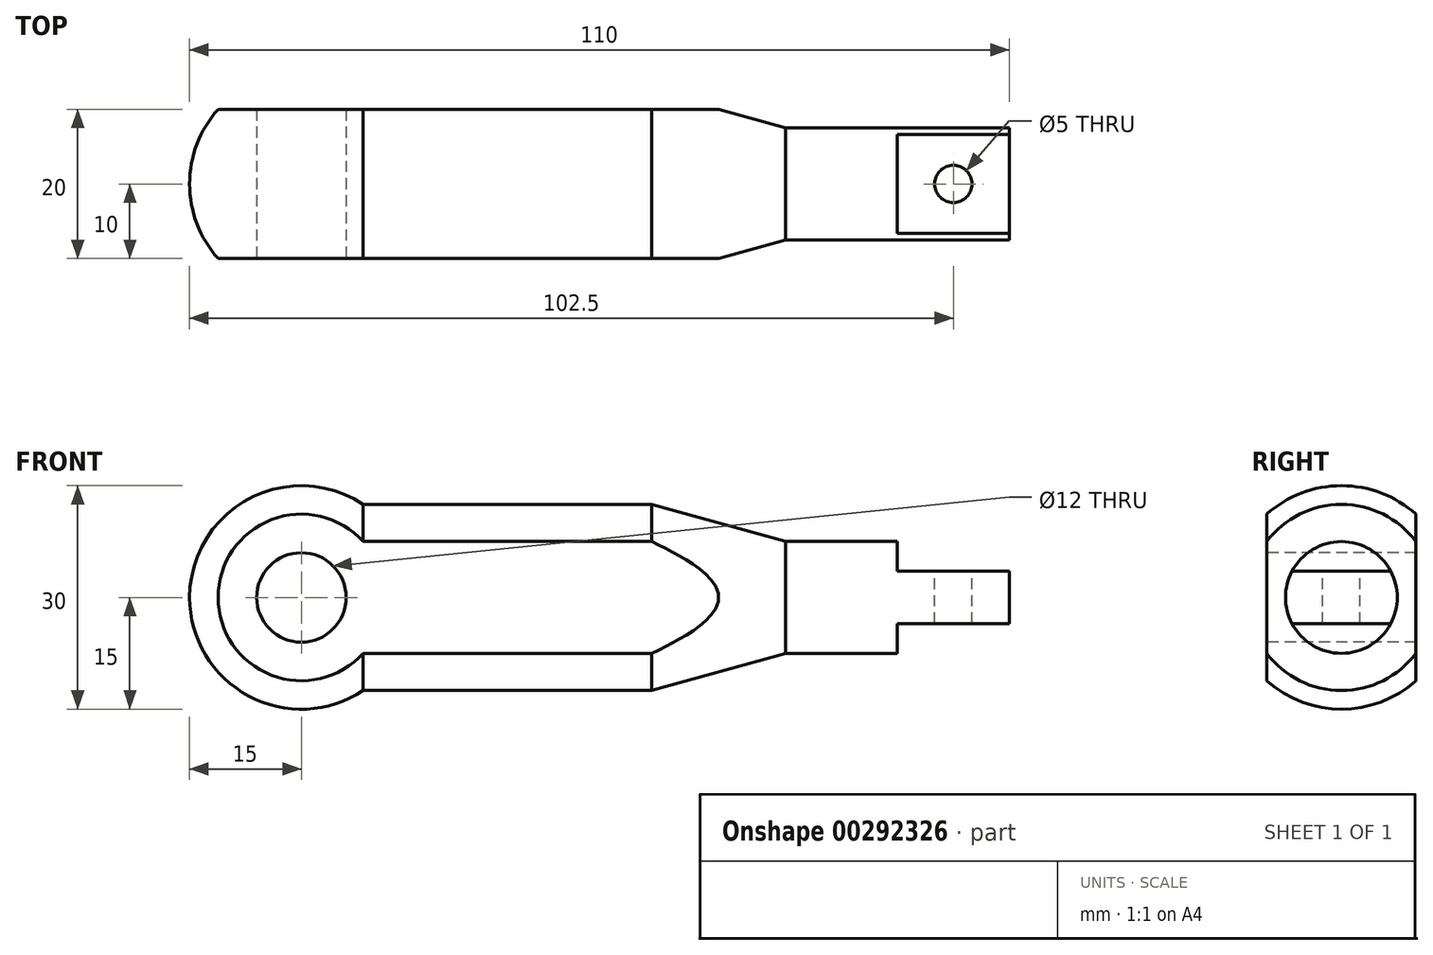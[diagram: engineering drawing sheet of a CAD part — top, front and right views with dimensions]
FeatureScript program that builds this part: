
annotation { "Feature Type Name" : "Feature", "Feature Type Description" : "" }
export const myFeature = defineFeature(function(context is Context, id is Id, definition is map)
    precondition{}
    {
        {
            var Q0;
            Q0=qCreatedBy(makeId("Front.planeOp"),FACE);
            var sketch = newSketch(context, id + "F0", { "sketchPlane" : qUnion([Q0])});
            skLineSegment(sketch, "E0", {"start": v(0, 0) * mm, "end": v(73.31, 0) * mm, "construction": true});
            skArc(sketch, "E1", {"start": v(-15, 0) * mm, "mid": v(-7.1, 13.22) * mm, "end": v(8.3, 12.5) * mm});
            skLineSegment(sketch, "E2", {"start": v(95, 7.5) * mm, "end": v(95, 0) * mm});
            skLineSegment(sketch, "E3", {"start": v(95, 0) * mm, "end": v(-15, 0) * mm});
            skLineSegment(sketch, "E4", {"start": v(8.3, 12.5) * mm, "end": v(47, 12.5) * mm});
            skLineSegment(sketch, "E5", {"start": v(47, 12.5) * mm, "end": v(65, 7.5) * mm});
            skLineSegment(sketch, "E6", {"start": v(65, 7.5) * mm, "end": v(95, 7.5) * mm});
            skSolve(sketch);
        }
        {
            var Q0;
            Q0 = qSketchRegion(id + "F0", true);
            var Q1;
            Q1=sQuery(id+"F0.wireOp",EDGE,"E3");
            revolve(context, id + "F1", {"entities" : qUnion([Q0]), "axis" : qUnion([Q1]), "revolveType" : RevolveType.FULL});
        }
        {
            var Q0;
            Q0=qCreatedBy(makeId("Front.planeOp"),FACE);
            var sketch = newSketch(context, id + "F2", { "sketchPlane" : qUnion([Q0])});
            skLineSegment(sketch, "E7.top", {"start": v(95, 3.5) * mm, "end": v(80, 3.5) * mm});
            skLineSegment(sketch, "E7.left", {"start": v(95, 7.5) * mm, "end": v(95, 3.5) * mm});
            skLineSegment(sketch, "E7.right", {"start": v(80, 7.5) * mm, "end": v(80, 3.5) * mm});
            skLineSegment(sketch, "E8", {"start": v(95, -7.5) * mm, "end": v(65, -7.5) * mm});
            skLineSegment(sketch, "E9", {"start": v(65, 7.5) * mm, "end": v(95, 7.5) * mm});
            skLineSegment(sketch, "E10", {"start": v(80, 7.5) * mm, "end": v(95, 7.5) * mm});
            skLineSegment(sketch, "E11", {"start": v(74.8, 0) * mm, "end": v(95.87, 0) * mm});
            skLineSegment(sketch, "E12.MirrorCS", {"start": v(95, -3.5) * mm, "end": v(80, -3.5) * mm});
            skLineSegment(sketch, "E13.MirrorCS", {"start": v(80, -7.5) * mm, "end": v(80, -3.5) * mm});
            skLineSegment(sketch, "E14.MirrorCS", {"start": v(95, -7.5) * mm, "end": v(95, -3.5) * mm});
            skLineSegment(sketch, "E15.MirrorCS", {"start": v(80, -7.5) * mm, "end": v(95, -7.5) * mm});
            skSolve(sketch);
        }
        {
            var Q0;
            Q0 = qSketchRegion(id + "F2", true);
            extrude(context, id + "F3", {"entities" : qUnion([Q0]), "operationType" : NewBodyOperationType.REMOVE, "endBound" : BoundingType.THROUGH_ALL, "oppositeDirection" : true, "depth" : 25 * mm, "hasSecondDirection" : true, "secondDirectionBound" : SecondDirectionBoundingType.THROUGH_ALL, "secondDirectionOppositeDirection" : false, "secondDirectionDepth" : 25 * mm});
        }
        {
            var Q0;
            Q0=makeQuery(id+"F1.opRevolve","SWEPT_FACE",FACE,{"disambiguationData":[OSD([sQuery(id+"F0.wireOp",EDGE,"E2")])]});
            var sketch = newSketch(context, id + "F4", { "sketchPlane" : qUnion([Q0])});
            skLineSegment(sketch, "E16", {"start": v(-10, 11.18) * mm, "end": v(-10, -11.18) * mm});
            skCircle(sketch, "E17", {"center": v(0, 0) * mm, "radius": 15 * mm});
            skLineSegment(sketch, "E18", {"start": v(10, 11.18) * mm, "end": v(10, -11.18) * mm});
            skLineSegment(sketch, "E19", {"start": v(0, 19.8) * mm, "end": v(0, -19.84) * mm, "construction": true});
            skArc(sketch, "E20", {"start": v(-10, 11.18) * mm, "mid": v(-15, 0) * mm, "end": v(-10, -11.18) * mm});
            skArc(sketch, "E21", {"start": v(10, -11.18) * mm, "mid": v(15, 0) * mm, "end": v(10, 11.18) * mm});
            skSolve(sketch);
        }
        {
            var Q0;
            {var subQ0=sQuery(id+"F4.wireOp",EDGE,"E16");Q0=makeQuery(id+"F4.imprint","IMPRINT",FACE,{"disambiguationData":[TD([[makeQuery(id+"F4.imprint","IMPRINT",EDGE,{"derivedFrom":subQ0}),-1.0]])]});}
            var Q1;
            {var subQ0=sQuery(id+"F4.wireOp",EDGE,"E18");Q1=makeQuery(id+"F4.imprint","IMPRINT",FACE,{"disambiguationData":[TD([[makeQuery(id+"F4.imprint","IMPRINT",EDGE,{"derivedFrom":subQ0}),1.0]])]});}
            var Q2;
            Q2=sQuery(id+"F4.wireOp",EDGE,"E21");
            var Q3;
            Q3=sQuery(id+"F4.wireOp",EDGE,"E18");
            var Q4;
            Q4=sQuery(id+"F4.wireOp",EDGE,"E16");
            var Q5;
            Q5=sQuery(id+"F4.wireOp",EDGE,"E20");
            extrude(context, id + "F5", {"entities" : qUnion([Q0, Q1]), "operationType" : NewBodyOperationType.REMOVE, "surfaceEntities" : qUnion([Q2, Q3, Q4, Q5]), "endBound" : BoundingType.THROUGH_ALL, "oppositeDirection" : true, "depth" : 25 * mm});
        }
        {
            var Q0;
            Q0=makeQuery(id+"F5.boolean.opBoolean","COPY",FACE,{"derivedFrom":makeQuery(id+"F5.opExtrude","SWEPT_FACE",FACE,{"disambiguationData":[OSD([sQuery(id+"F4.wireOp",EDGE,"E16")])]})});
            var sketch = newSketch(context, id + "F6", { "sketchPlane" : qUnion([Q0])});
            skCircle(sketch, "E22", {"center": v(0, 0) * mm, "radius": 6 * mm});
            skSolve(sketch);
        }
        {
            var Q0;
            Q0 = qSketchRegion(id + "F6", true);
            extrude(context, id + "F7", {"entities" : qUnion([Q0]), "operationType" : NewBodyOperationType.REMOVE, "endBound" : BoundingType.THROUGH_ALL, "oppositeDirection" : true, "depth" : 25 * mm});
        }
        {
            var Q0;
            Q0=makeQuery(id+"F3.boolean.opBoolean","COPY",FACE,{"derivedFrom":makeQuery(id+"F3.opExtrude","SWEPT_FACE",FACE,{"disambiguationData":[OSD([sQuery(id+"F2.wireOp",EDGE,"E7.top")])]})});
            var sketch = newSketch(context, id + "F8", { "sketchPlane" : qUnion([Q0])});
            skCircle(sketch, "E23", {"center": v(87.5, 0) * mm, "radius": 2.5 * mm});
            skSolve(sketch);
        }
        {
            var Q0;
            Q0 = qSketchRegion(id + "F8", true);
            extrude(context, id + "F9", {"entities" : qUnion([Q0]), "operationType" : NewBodyOperationType.REMOVE, "endBound" : BoundingType.THROUGH_ALL, "oppositeDirection" : true, "depth" : 25 * mm});
        }
    });
